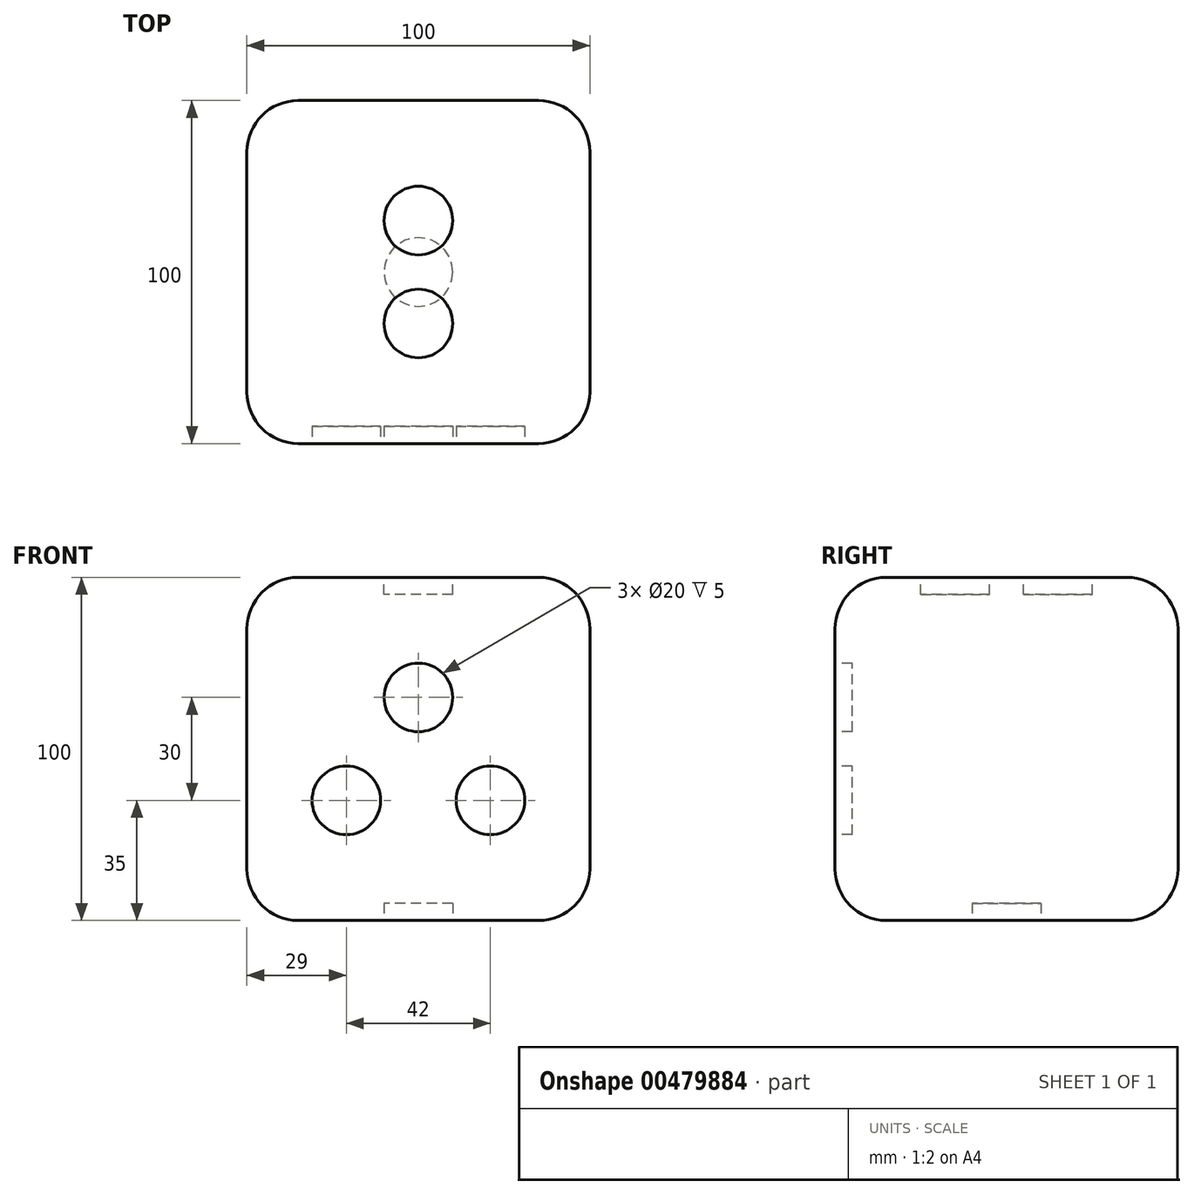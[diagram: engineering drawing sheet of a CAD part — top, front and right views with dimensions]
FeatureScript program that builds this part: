
annotation { "Feature Type Name" : "Feature", "Feature Type Description" : "" }
export const myFeature = defineFeature(function(context is Context, id is Id, definition is map)
    precondition{}
    {
        {
            var Q0;
            Q0=qCreatedBy(makeId("Top.planeOp"),FACE);
            var sketch = newSketch(context, id + "F0", { "sketchPlane" : qUnion([Q0])});
            skLineSegment(sketch, "E0.bottom", {"start": v(-76.76, 73.37) * mm, "end": v(75.4, 73.37) * mm});
            skLineSegment(sketch, "E0.top", {"start": v(-76.76, -75.63) * mm, "end": v(75.4, -75.63) * mm});
            skLineSegment(sketch, "E0.left", {"start": v(-76.76, 73.37) * mm, "end": v(-76.76, -75.63) * mm});
            skLineSegment(sketch, "E0.right", {"start": v(75.4, 73.37) * mm, "end": v(75.4, -75.63) * mm});
            skLineSegment(sketch, "E1.bottom", {"start": v(-50, 50) * mm, "end": v(50, 50) * mm});
            skLineSegment(sketch, "E1.top", {"start": v(-50, -50) * mm, "end": v(50, -50) * mm});
            skLineSegment(sketch, "E1.left", {"start": v(-50, 50) * mm, "end": v(-50, -50) * mm});
            skLineSegment(sketch, "E1.right", {"start": v(50, 50) * mm, "end": v(50, -50) * mm});
            skPoint(sketch, "E1.middle", {"position": v(0, 0) * mm});
            skSolve(sketch);
        }
        {
            var Q0;
            Q0=makeQuery(id+"F0.imprint","IMPRINT",FACE,{"disambiguationData":[TD([[makeQuery(id+"F0.imprint","IMPRINT",EDGE,{"derivedFrom":sQuery(id+"F0.wireOp",EDGE,"E1.bottom")}),-1.0]])]});
            extrude(context, id + "F1", {"entities" : qUnion([Q0]), "depth" : 100 * mm});
        }
        {
            var Q0;
            Q0=makeQuery(id+"F1.opExtrude","SWEPT_EDGE",EDGE,{"disambiguationData":[OSD([sQuery(id+"F0.wireOp",EDGE,"E1.bottom"),sQuery(id+"F0.wireOp",EDGE,"E1.right")])]});
            var Q1;
            Q1=makeQuery(id+"F1.opExtrude","CAP_EDGE",EDGE,{"disambiguationData":[OSD([sQuery(id+"F0.wireOp",EDGE,"E1.bottom")])],"isStart":false});
            var Q2;
            Q2=makeQuery(id+"F1.opExtrude","CAP_EDGE",EDGE,{"disambiguationData":[OSD([sQuery(id+"F0.wireOp",EDGE,"E1.right")])],"isStart":false});
            var Q3;
            Q3=makeQuery(id+"F1.opExtrude","SWEPT_FACE",FACE,{"disambiguationData":[OSD([sQuery(id+"F0.wireOp",EDGE,"E1.left")])]});
            fillet(context, id + "F2", {"entities" : qUnion([Q0, Q1, Q2, Q3]), "radius" : 15 * mm, "tangentPropagation" : true, "allowEdgeOverflow" : false});
        }
        {
            var Q0;
            {var subQ0=sQuery(id+"F0.wireOp",EDGE,"E1.left");var subQ1=sQuery(id+"F0.wireOp",EDGE,"E1.bottom");Q0=makeQuery(id+"F2.opFillet","BLEND_FACE",FACE,{"disambiguationData":[OSD([subQ1,subQ0]),TDD([makeQuery(id+"F1.opExtrude","SWEPT_EDGE",EDGE,{"disambiguationData":[OSD([subQ1,subQ0])]})])]});}
            var Q1;
            Q1=makeQuery(id+"F2.opFillet","BLEND_FACE",FACE,{"disambiguationData":[OSD([sQuery(id+"F0.wireOp",EDGE,"E1.bottom")])]});
            var Q2;
            Q2=makeQuery(id+"F1.opExtrude","CAP_FACE",FACE,{"disambiguationData":[OSD([sQuery(id+"F0.wireOp",EDGE,"E1.bottom"),sQuery(id+"F0.wireOp",EDGE,"E1.top"),sQuery(id+"F0.wireOp",EDGE,"E1.left"),sQuery(id+"F0.wireOp",EDGE,"E1.right")])],"isStart":false});
            var Q3;
            Q3=makeQuery(id+"F1.opExtrude","SWEPT_FACE",FACE,{"disambiguationData":[OSD([sQuery(id+"F0.wireOp",EDGE,"E1.right")])]});
            var Q4;
            Q4=makeQuery(id+"F2.opFillet","BLEND_FACE",FACE,{"disambiguationData":[OSD([sQuery(id+"F0.wireOp",EDGE,"E1.right")])]});
            var Q5;
            {var subQ0=sQuery(id+"F0.wireOp",EDGE,"E1.right");Q5=makeQuery(id+"F2.opFillet","BLEND_EDGE",EDGE,{"blendedFrom":[makeQuery(id+"F1.opExtrude","CAP_EDGE",EDGE,{"disambiguationData":[OSD([subQ0])],"isStart":false}),makeQuery(id+"F1.opExtrude","SWEPT_FACE",FACE,{"disambiguationData":[OSD([subQ0])]})],"blendedInto":[makeQuery(id+"F1.opExtrude","SWEPT_FACE",FACE,{"disambiguationData":[OSD([subQ0])]})]});}
            var Q6;
            Q6=makeQuery(id+"F1.opExtrude","SWEPT_FACE",FACE,{"disambiguationData":[OSD([sQuery(id+"F0.wireOp",EDGE,"E1.left")])]});
            var Q7;
            {var subQ0=sQuery(id+"F0.wireOp",EDGE,"E1.left");var subQ1=sQuery(id+"F0.wireOp",EDGE,"E1.bottom");Q7=makeQuery(id+"F2.opFillet","BLEND_FACE",FACE,{"disambiguationData":[OSD([subQ1,subQ0]),TDD([makeQuery(id+"F1.opExtrude","CAP_VERTEX",VERTEX,{"disambiguationData":[OSD([subQ1,subQ0])],"isStart":false})])]});}
            var Q8;
            {var subQ0=sQuery(id+"F0.wireOp",EDGE,"E1.left");Q8=makeQuery(id+"F2.opFillet","BLEND_FACE",FACE,{"disambiguationData":[OSD([subQ0]),TDD([makeQuery(id+"F1.opExtrude","CAP_EDGE",EDGE,{"disambiguationData":[OSD([subQ0])],"isStart":false})])]});}
            var Q9;
            {var subQ0=sQuery(id+"F0.wireOp",EDGE,"E1.left");Q9=makeQuery(id+"F2.opFillet","BLEND_EDGE",EDGE,{"blendedFrom":[makeQuery(id+"F1.opExtrude","CAP_EDGE",EDGE,{"disambiguationData":[OSD([subQ0])],"isStart":false}),makeQuery(id+"F1.opExtrude","SWEPT_FACE",FACE,{"disambiguationData":[OSD([subQ0])]})],"blendedInto":[makeQuery(id+"F1.opExtrude","SWEPT_FACE",FACE,{"disambiguationData":[OSD([subQ0])]})]});}
            var Q10;
            {var subQ0=sQuery(id+"F0.wireOp",EDGE,"E1.left");var subQ1=sQuery(id+"F0.wireOp",EDGE,"E1.bottom");Q10=makeQuery(id+"F2.opFillet","BLEND_EDGE",EDGE,{"blendedFrom":[makeQuery(id+"F1.opExtrude","CAP_VERTEX",VERTEX,{"disambiguationData":[OSD([subQ1,subQ0])],"isStart":false}),makeQuery(id+"F1.opExtrude","SWEPT_EDGE",EDGE,{"disambiguationData":[OSD([subQ1,subQ0])]})],"blendedInto":[]});}
            var Q11;
            {var subQ0=sQuery(id+"F0.wireOp",EDGE,"E1.bottom");Q11=makeQuery(id+"F2.opFillet","BLEND_EDGE",EDGE,{"blendedFrom":[makeQuery(id+"F1.opExtrude","CAP_VERTEX",VERTEX,{"disambiguationData":[OSD([subQ0,sQuery(id+"F0.wireOp",EDGE,"E1.left")])],"isStart":false}),makeQuery(id+"F1.opExtrude","CAP_EDGE",EDGE,{"disambiguationData":[OSD([subQ0])],"isStart":false})],"blendedInto":[]});}
            var Q12;
            {var subQ0=sQuery(id+"F0.wireOp",EDGE,"E1.left");Q12=makeQuery(id+"F2.opFillet","BLEND_EDGE",EDGE,{"blendedFrom":[makeQuery(id+"F1.opExtrude","CAP_VERTEX",VERTEX,{"disambiguationData":[OSD([sQuery(id+"F0.wireOp",EDGE,"E1.bottom"),subQ0])],"isStart":false}),makeQuery(id+"F1.opExtrude","CAP_EDGE",EDGE,{"disambiguationData":[OSD([subQ0])],"isStart":false})],"blendedInto":[]});}
            var Q13;
            {var subQ0=sQuery(id+"F0.wireOp",EDGE,"E1.bottom");Q13=makeQuery(id+"F2.opFillet","BLEND_EDGE",EDGE,{"blendedFrom":[makeQuery(id+"F1.opExtrude","SWEPT_EDGE",EDGE,{"disambiguationData":[OSD([subQ0,sQuery(id+"F0.wireOp",EDGE,"E1.left")])]}),makeQuery(id+"F1.opExtrude","SWEPT_FACE",FACE,{"disambiguationData":[OSD([subQ0])]})],"blendedInto":[makeQuery(id+"F1.opExtrude","SWEPT_FACE",FACE,{"disambiguationData":[OSD([subQ0])]})]});}
            var Q14;
            {var subQ0=sQuery(id+"F0.wireOp",EDGE,"E1.left");Q14=makeQuery(id+"F2.opFillet","BLEND_EDGE",EDGE,{"blendedFrom":[makeQuery(id+"F1.opExtrude","SWEPT_EDGE",EDGE,{"disambiguationData":[OSD([sQuery(id+"F0.wireOp",EDGE,"E1.bottom"),subQ0])]}),makeQuery(id+"F1.opExtrude","SWEPT_FACE",FACE,{"disambiguationData":[OSD([subQ0])]})],"blendedInto":[makeQuery(id+"F1.opExtrude","SWEPT_FACE",FACE,{"disambiguationData":[OSD([subQ0])]})]});}
            var Q15;
            {var subQ0=sQuery(id+"F0.wireOp",EDGE,"E1.bottom");Q15=makeQuery(id+"F2.opFillet","BLEND_EDGE",EDGE,{"blendedFrom":[makeQuery(id+"F1.opExtrude","CAP_EDGE",EDGE,{"disambiguationData":[OSD([subQ0])],"isStart":false}),makeQuery(id+"F1.opExtrude","SWEPT_FACE",FACE,{"disambiguationData":[OSD([subQ0])]})],"blendedInto":[makeQuery(id+"F1.opExtrude","SWEPT_FACE",FACE,{"disambiguationData":[OSD([subQ0])]})]});}
            var Q16;
            Q16=makeQuery(id+"F1.opExtrude","CAP_FACE",FACE,{"disambiguationData":[OSD([sQuery(id+"F0.wireOp",EDGE,"E1.bottom"),sQuery(id+"F0.wireOp",EDGE,"E1.top"),sQuery(id+"F0.wireOp",EDGE,"E1.left"),sQuery(id+"F0.wireOp",EDGE,"E1.right")])],"isStart":true});
            var Q17;
            Q17=makeQuery(id+"F1.opExtrude","SWEPT_FACE",FACE,{"disambiguationData":[OSD([sQuery(id+"F0.wireOp",EDGE,"E1.top")])]});
            var Q18;
            Q18=makeQuery(id+"F1.opExtrude","CAP_EDGE",EDGE,{"disambiguationData":[OSD([sQuery(id+"F0.wireOp",EDGE,"E1.top")])],"isStart":true});
            var Q19;
            Q19=makeQuery(id+"F1.opExtrude","SWEPT_EDGE",EDGE,{"disambiguationData":[OSD([sQuery(id+"F0.wireOp",EDGE,"E1.top"),sQuery(id+"F0.wireOp",EDGE,"E1.right")])]});
            var Q20;
            Q20=makeQuery(id+"F1.opExtrude","CAP_EDGE",EDGE,{"disambiguationData":[OSD([sQuery(id+"F0.wireOp",EDGE,"E1.right")])],"isStart":true});
            var Q21;
            {var subQ0=sQuery(id+"F0.wireOp",EDGE,"E1.right");var subQ1=sQuery(id+"F0.wireOp",EDGE,"E1.bottom");Q21=makeQuery(id+"F2.opFillet","BLEND_FACE",FACE,{"disambiguationData":[OSD([subQ1,subQ0]),TDD([makeQuery(id+"F1.opExtrude","CAP_VERTEX",VERTEX,{"disambiguationData":[OSD([subQ1,subQ0])],"isStart":false})])]});}
            var Q22;
            {var subQ0=sQuery(id+"F0.wireOp",EDGE,"E1.bottom");Q22=makeQuery(id+"F2.opFillet","BLEND_EDGE",EDGE,{"blendedFrom":[makeQuery(id+"F1.opExtrude","CAP_VERTEX",VERTEX,{"disambiguationData":[OSD([subQ0,sQuery(id+"F0.wireOp",EDGE,"E1.right")])],"isStart":false}),makeQuery(id+"F1.opExtrude","CAP_EDGE",EDGE,{"disambiguationData":[OSD([subQ0])],"isStart":false})],"blendedInto":[]});}
            var Q23;
            {var subQ0=sQuery(id+"F0.wireOp",EDGE,"E1.left");Q23=makeQuery(id+"F2.opFillet","BLEND_FACE",FACE,{"disambiguationData":[OSD([subQ0]),TDD([makeQuery(id+"F1.opExtrude","CAP_EDGE",EDGE,{"disambiguationData":[OSD([subQ0])],"isStart":true})])]});}
            var Q24;
            Q24=makeQuery(id+"F1.opExtrude","SWEPT_FACE",FACE,{"disambiguationData":[OSD([sQuery(id+"F0.wireOp",EDGE,"E1.bottom")])]});
            var Q25;
            {var subQ0=sQuery(id+"F0.wireOp",EDGE,"E1.left");Q25=makeQuery(id+"F2.opFillet","BLEND_EDGE",EDGE,{"blendedFrom":[makeQuery(id+"F1.opExtrude","CAP_EDGE",EDGE,{"disambiguationData":[OSD([subQ0])],"isStart":true}),makeQuery(id+"F1.opExtrude","SWEPT_FACE",FACE,{"disambiguationData":[OSD([subQ0])]})],"blendedInto":[makeQuery(id+"F1.opExtrude","SWEPT_FACE",FACE,{"disambiguationData":[OSD([subQ0])]})]});}
            var Q26;
            {var subQ0=sQuery(id+"F0.wireOp",EDGE,"E1.right");var subQ1=sQuery(id+"F0.wireOp",EDGE,"E1.bottom");Q26=makeQuery(id+"F2.opFillet","BLEND_FACE",FACE,{"disambiguationData":[OSD([subQ1,subQ0]),TDD([makeQuery(id+"F1.opExtrude","SWEPT_EDGE",EDGE,{"disambiguationData":[OSD([subQ1,subQ0])]})])]});}
            var Q27;
            {var subQ0=sQuery(id+"F0.wireOp",EDGE,"E1.right");Q27=makeQuery(id+"F2.opFillet","BLEND_EDGE",EDGE,{"blendedFrom":[makeQuery(id+"F1.opExtrude","CAP_VERTEX",VERTEX,{"disambiguationData":[OSD([sQuery(id+"F0.wireOp",EDGE,"E1.bottom"),subQ0])],"isStart":false}),makeQuery(id+"F1.opExtrude","CAP_EDGE",EDGE,{"disambiguationData":[OSD([subQ0])],"isStart":false})],"blendedInto":[]});}
            var Q28;
            {var subQ0=sQuery(id+"F0.wireOp",EDGE,"E1.left");Q28=makeQuery(id+"F2.opFillet","BLEND_EDGE",EDGE,{"blendedFrom":[makeQuery(id+"F1.opExtrude","SWEPT_EDGE",EDGE,{"disambiguationData":[OSD([sQuery(id+"F0.wireOp",EDGE,"E1.bottom"),subQ0])]}),makeQuery(id+"F1.opExtrude","CAP_EDGE",EDGE,{"disambiguationData":[OSD([subQ0])],"isStart":true})],"blendedInto":[]});}
            var Q29;
            Q29=makeQuery(id+"F1.opExtrude","CAP_EDGE",EDGE,{"disambiguationData":[OSD([sQuery(id+"F0.wireOp",EDGE,"E1.bottom")])],"isStart":true});
            var Q30;
            {var subQ0=sQuery(id+"F0.wireOp",EDGE,"E1.bottom");Q30=makeQuery(id+"F2.opFillet","BLEND_EDGE",EDGE,{"blendedFrom":[makeQuery(id+"F1.opExtrude","CAP_EDGE",EDGE,{"disambiguationData":[OSD([subQ0])],"isStart":false}),makeQuery(id+"F1.opExtrude","CAP_FACE",FACE,{"disambiguationData":[OSD([subQ0,sQuery(id+"F0.wireOp",EDGE,"E1.top"),sQuery(id+"F0.wireOp",EDGE,"E1.left"),sQuery(id+"F0.wireOp",EDGE,"E1.right")])],"isStart":false})],"blendedInto":[makeQuery(id+"F1.opExtrude","CAP_FACE",FACE,{"disambiguationData":[OSD([subQ0,sQuery(id+"F0.wireOp",EDGE,"E1.top"),sQuery(id+"F0.wireOp",EDGE,"E1.left"),sQuery(id+"F0.wireOp",EDGE,"E1.right")])],"isStart":false})]});}
            var Q31;
            Q31=makeQuery(id+"F1.opExtrude","CAP_EDGE",EDGE,{"disambiguationData":[OSD([sQuery(id+"F0.wireOp",EDGE,"E1.top")])],"isStart":false});
            var Q32;
            {var subQ0=sQuery(id+"F0.wireOp",EDGE,"E1.left");Q32=makeQuery(id+"F2.opFillet","BLEND_EDGE",EDGE,{"blendedFrom":[makeQuery(id+"F1.opExtrude","CAP_EDGE",EDGE,{"disambiguationData":[OSD([subQ0])],"isStart":false}),makeQuery(id+"F1.opExtrude","CAP_FACE",FACE,{"disambiguationData":[OSD([sQuery(id+"F0.wireOp",EDGE,"E1.bottom"),sQuery(id+"F0.wireOp",EDGE,"E1.top"),subQ0,sQuery(id+"F0.wireOp",EDGE,"E1.right")])],"isStart":false})],"blendedInto":[makeQuery(id+"F1.opExtrude","CAP_FACE",FACE,{"disambiguationData":[OSD([sQuery(id+"F0.wireOp",EDGE,"E1.bottom"),sQuery(id+"F0.wireOp",EDGE,"E1.top"),subQ0,sQuery(id+"F0.wireOp",EDGE,"E1.right")])],"isStart":false})]});}
            var Q33;
            {var subQ0=sQuery(id+"F0.wireOp",EDGE,"E1.right");Q33=makeQuery(id+"F2.opFillet","BLEND_EDGE",EDGE,{"blendedFrom":[makeQuery(id+"F1.opExtrude","CAP_EDGE",EDGE,{"disambiguationData":[OSD([subQ0])],"isStart":false}),makeQuery(id+"F1.opExtrude","CAP_FACE",FACE,{"disambiguationData":[OSD([sQuery(id+"F0.wireOp",EDGE,"E1.bottom"),sQuery(id+"F0.wireOp",EDGE,"E1.top"),sQuery(id+"F0.wireOp",EDGE,"E1.left"),subQ0])],"isStart":false})],"blendedInto":[makeQuery(id+"F1.opExtrude","CAP_FACE",FACE,{"disambiguationData":[OSD([sQuery(id+"F0.wireOp",EDGE,"E1.bottom"),sQuery(id+"F0.wireOp",EDGE,"E1.top"),sQuery(id+"F0.wireOp",EDGE,"E1.left"),subQ0])],"isStart":false})]});}
            var Q34;
            {var subQ0=sQuery(id+"F0.wireOp",EDGE,"E1.right");var subQ1=sQuery(id+"F0.wireOp",EDGE,"E1.bottom");Q34=makeQuery(id+"F2.opFillet","BLEND_EDGE",EDGE,{"blendedFrom":[makeQuery(id+"F1.opExtrude","SWEPT_EDGE",EDGE,{"disambiguationData":[OSD([subQ1,subQ0])]}),makeQuery(id+"F1.opExtrude","CAP_FACE",FACE,{"disambiguationData":[OSD([subQ1,sQuery(id+"F0.wireOp",EDGE,"E1.top"),sQuery(id+"F0.wireOp",EDGE,"E1.left"),subQ0])],"isStart":true})],"blendedInto":[makeQuery(id+"F1.opExtrude","CAP_FACE",FACE,{"disambiguationData":[OSD([subQ1,sQuery(id+"F0.wireOp",EDGE,"E1.top"),sQuery(id+"F0.wireOp",EDGE,"E1.left"),subQ0])],"isStart":true})]});}
            var Q35;
            {var subQ0=sQuery(id+"F0.wireOp",EDGE,"E1.right");Q35=makeQuery(id+"F2.opFillet","BLEND_EDGE",EDGE,{"blendedFrom":[makeQuery(id+"F1.opExtrude","SWEPT_EDGE",EDGE,{"disambiguationData":[OSD([sQuery(id+"F0.wireOp",EDGE,"E1.bottom"),subQ0])]}),makeQuery(id+"F1.opExtrude","SWEPT_FACE",FACE,{"disambiguationData":[OSD([subQ0])]})],"blendedInto":[makeQuery(id+"F1.opExtrude","SWEPT_FACE",FACE,{"disambiguationData":[OSD([subQ0])]})]});}
            var Q36;
            {var subQ0=sQuery(id+"F0.wireOp",EDGE,"E1.left");Q36=makeQuery(id+"F2.opFillet","BLEND_EDGE",EDGE,{"blendedFrom":[makeQuery(id+"F1.opExtrude","CAP_EDGE",EDGE,{"disambiguationData":[OSD([subQ0])],"isStart":true}),makeQuery(id+"F1.opExtrude","CAP_FACE",FACE,{"disambiguationData":[OSD([sQuery(id+"F0.wireOp",EDGE,"E1.bottom"),sQuery(id+"F0.wireOp",EDGE,"E1.top"),subQ0,sQuery(id+"F0.wireOp",EDGE,"E1.right")])],"isStart":true})],"blendedInto":[makeQuery(id+"F1.opExtrude","CAP_FACE",FACE,{"disambiguationData":[OSD([sQuery(id+"F0.wireOp",EDGE,"E1.bottom"),sQuery(id+"F0.wireOp",EDGE,"E1.top"),subQ0,sQuery(id+"F0.wireOp",EDGE,"E1.right")])],"isStart":true})]});}
            var Q37;
            Q37=makeQuery(id+"F2.opFillet","BLEND_EDGE",EDGE,{"blendedFrom":[makeQuery(id+"F1.opExtrude","CAP_EDGE",EDGE,{"disambiguationData":[OSD([sQuery(id+"F0.wireOp",EDGE,"E1.right")])],"isStart":false}),makeQuery(id+"F1.opExtrude","SWEPT_FACE",FACE,{"disambiguationData":[OSD([sQuery(id+"F0.wireOp",EDGE,"E1.top")])]})],"blendedInto":[makeQuery(id+"F1.opExtrude","SWEPT_FACE",FACE,{"disambiguationData":[OSD([sQuery(id+"F0.wireOp",EDGE,"E1.top")])]})]});
            var Q38;
            Q38=makeQuery(id+"F2.opFillet","BLEND_FACE",FACE,{"disambiguationData":[OSD([sQuery(id+"F0.wireOp",EDGE,"E1.top"),sQuery(id+"F0.wireOp",EDGE,"E1.left")])]});
            var Q39;
            {var subQ0=sQuery(id+"F0.wireOp",EDGE,"E1.left");Q39=makeQuery(id+"F2.opFillet","BLEND_EDGE",EDGE,{"blendedFrom":[makeQuery(id+"F1.opExtrude","SWEPT_EDGE",EDGE,{"disambiguationData":[OSD([sQuery(id+"F0.wireOp",EDGE,"E1.top"),subQ0])]}),makeQuery(id+"F1.opExtrude","CAP_EDGE",EDGE,{"disambiguationData":[OSD([subQ0])],"isStart":false})],"blendedInto":[]});}
            var Q40;
            {var subQ0=sQuery(id+"F0.wireOp",EDGE,"E1.left");Q40=makeQuery(id+"F2.opFillet","BLEND_EDGE",EDGE,{"blendedFrom":[makeQuery(id+"F1.opExtrude","SWEPT_EDGE",EDGE,{"disambiguationData":[OSD([sQuery(id+"F0.wireOp",EDGE,"E1.top"),subQ0])]}),makeQuery(id+"F1.opExtrude","SWEPT_FACE",FACE,{"disambiguationData":[OSD([subQ0])]})],"blendedInto":[makeQuery(id+"F1.opExtrude","SWEPT_FACE",FACE,{"disambiguationData":[OSD([subQ0])]})]});}
            var Q41;
            {var subQ0=sQuery(id+"F0.wireOp",EDGE,"E1.top");Q41=makeQuery(id+"F2.opFillet","BLEND_EDGE",EDGE,{"blendedFrom":[makeQuery(id+"F1.opExtrude","SWEPT_EDGE",EDGE,{"disambiguationData":[OSD([subQ0,sQuery(id+"F0.wireOp",EDGE,"E1.left")])]}),makeQuery(id+"F1.opExtrude","SWEPT_FACE",FACE,{"disambiguationData":[OSD([subQ0])]})],"blendedInto":[makeQuery(id+"F1.opExtrude","SWEPT_FACE",FACE,{"disambiguationData":[OSD([subQ0])]})]});}
            var Q42;
            {var subQ0=sQuery(id+"F0.wireOp",EDGE,"E1.left");Q42=makeQuery(id+"F2.opFillet","BLEND_EDGE",EDGE,{"blendedFrom":[makeQuery(id+"F1.opExtrude","SWEPT_EDGE",EDGE,{"disambiguationData":[OSD([sQuery(id+"F0.wireOp",EDGE,"E1.top"),subQ0])]}),makeQuery(id+"F1.opExtrude","CAP_EDGE",EDGE,{"disambiguationData":[OSD([subQ0])],"isStart":true})],"blendedInto":[]});}
            fillet(context, id + "F3", {"entities" : qUnion([Q0, Q1, Q2, Q3, Q4, Q5, Q6, Q7, Q8, Q9, Q10, Q11, Q12, Q13, Q14, Q15, Q16, Q17, Q18, Q19, Q20, Q21, Q22, Q23, Q24, Q25, Q26, Q27, Q28, Q29, Q30, Q31, Q32, Q33, Q34, Q35, Q36, Q37, Q38, Q39, Q40, Q41, Q42]), "radius" : 15 * mm, "tangentPropagation" : true, "allowEdgeOverflow" : false});
        }
        {
            var Q0;
            Q0=qCreatedBy(makeId("Top.planeOp"),FACE);
            var sketch = newSketch(context, id + "F4", { "sketchPlane" : qUnion([Q0])});
            skCircle(sketch, "E2", {"center": v(0, 0) * mm, "radius": 10 * mm});
            skSolve(sketch);
        }
        {
            var Q0;
            Q0=makeQuery(id+"F4.imprint","IMPRINT",FACE,{"disambiguationData":[TD([[makeQuery(id+"F4.imprint","IMPRINT",EDGE,{"derivedFrom":sQuery(id+"F4.wireOp",EDGE,"E2")}),1.0]])]});
            var Q1;
            Q1=sQuery(id+"F4.wireOp",EDGE,"E2");
            extrude(context, id + "F5", {"entities" : qUnion([Q0]), "operationType" : NewBodyOperationType.REMOVE, "surfaceEntities" : qUnion([Q1]), "depth" : 5 * mm});
        }
        {
            var Q0;
            Q0=makeQuery(id+"F1.opExtrude","SWEPT_FACE",FACE,{"disambiguationData":[OSD([sQuery(id+"F0.wireOp",EDGE,"E1.right")])]});
            var sketch = newSketch(context, id + "F6", { "sketchPlane" : qUnion([Q0])});
            skSolve(sketch);
        }
        {
            var Q0;
            Q0=makeQuery(id+"F1.opExtrude","CAP_FACE",FACE,{"disambiguationData":[OSD([sQuery(id+"F0.wireOp",EDGE,"E1.bottom"),sQuery(id+"F0.wireOp",EDGE,"E1.top"),sQuery(id+"F0.wireOp",EDGE,"E1.left"),sQuery(id+"F0.wireOp",EDGE,"E1.right")])],"isStart":false});
            var sketch = newSketch(context, id + "F7", { "sketchPlane" : qUnion([Q0])});
            skCircle(sketch, "E3", {"center": v(0, -15) * mm, "radius": 10 * mm});
            skCircle(sketch, "E4", {"center": v(0, 15) * mm, "radius": 10 * mm});
            skSolve(sketch);
        }
        {
            var Q0;
            Q0 = qSketchRegion(id + "F7", true);
            extrude(context, id + "F8", {"entities" : qUnion([Q0]), "operationType" : NewBodyOperationType.REMOVE, "oppositeDirection" : true, "depth" : 5 * mm});
        }
        {
            var Q0;
            Q0=makeQuery(id+"F1.opExtrude","SWEPT_FACE",FACE,{"disambiguationData":[OSD([sQuery(id+"F0.wireOp",EDGE,"E1.top")])]});
            var sketch = newSketch(context, id + "F9", { "sketchPlane" : qUnion([Q0])});
            skCircle(sketch, "E5", {"center": v(0, 65) * mm, "radius": 10 * mm});
            skCircle(sketch, "E6", {"center": v(-21, 35) * mm, "radius": 10 * mm});
            skCircle(sketch, "E7", {"center": v(21, 35) * mm, "radius": 10 * mm});
            skSolve(sketch);
        }
        {
            var Q0;
            Q0=makeQuery(id+"F9.imprint","IMPRINT",FACE,{"disambiguationData":[TD([[makeQuery(id+"F9.imprint","IMPRINT",EDGE,{"derivedFrom":sQuery(id+"F9.wireOp",EDGE,"E5")}),1.0]])]});
            var Q1;
            Q1=makeQuery(id+"F9.imprint","IMPRINT",FACE,{"disambiguationData":[TD([[makeQuery(id+"F9.imprint","IMPRINT",EDGE,{"derivedFrom":sQuery(id+"F9.wireOp",EDGE,"E6")}),1.0]])]});
            var Q2;
            Q2=makeQuery(id+"F9.imprint","IMPRINT",FACE,{"disambiguationData":[TD([[makeQuery(id+"F9.imprint","IMPRINT",EDGE,{"derivedFrom":sQuery(id+"F9.wireOp",EDGE,"E7")}),1.0]])]});
            var Q3;
            Q3=sQuery(id+"F9.wireOp",EDGE,"E5");
            var Q4;
            Q4=sQuery(id+"F9.wireOp",EDGE,"E6");
            var Q5;
            Q5=sQuery(id+"F9.wireOp",EDGE,"E7");
            extrude(context, id + "F10", {"entities" : qUnion([Q0, Q1, Q2]), "operationType" : NewBodyOperationType.REMOVE, "surfaceEntities" : qUnion([Q3, Q4, Q5]), "oppositeDirection" : true, "depth" : 5 * mm});
        }
    });
